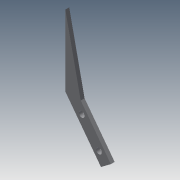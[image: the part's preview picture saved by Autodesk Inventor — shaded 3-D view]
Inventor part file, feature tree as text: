
AUTODESK INVENTOR PART (.ipt)
format: ipt  version: 2013 (Build 170138000, 138)  size: 75,776 bytes
history: native  units: mm
features: sketch x2, extrude x1
ambient origin geometry x8: Origin, YZ Plane, XZ Plane, XY Plane, X Axis, Y Axis, Z Axis, Center Point
bodies: Solid1 (feature_tree)
feature tree (3):
  sketch  "Sketch1"  dims[d4=3.0mm d5=3.0mm d6=2.0mm d7=0.0mm]
  extrude  "Extrusion1"  Depth=2.0mm TaperAngle=0.0deg
  sketch  "Sketch2"
